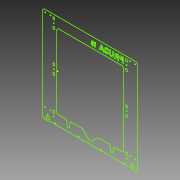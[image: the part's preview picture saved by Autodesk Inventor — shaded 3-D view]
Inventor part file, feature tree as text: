
AUTODESK INVENTOR PART (.ipt)
format: ipt  version: 2015 (Build 190159000, 159)  size: 310,272 bytes
history: native  units: mm
features: sketch x1
ambient origin geometry x8: Origin, YZ Plane, XZ Plane, XY Plane, X Axis, Y Axis, Z Axis, Center Point
feature tree (1):
  sketch  "Sketch1"
